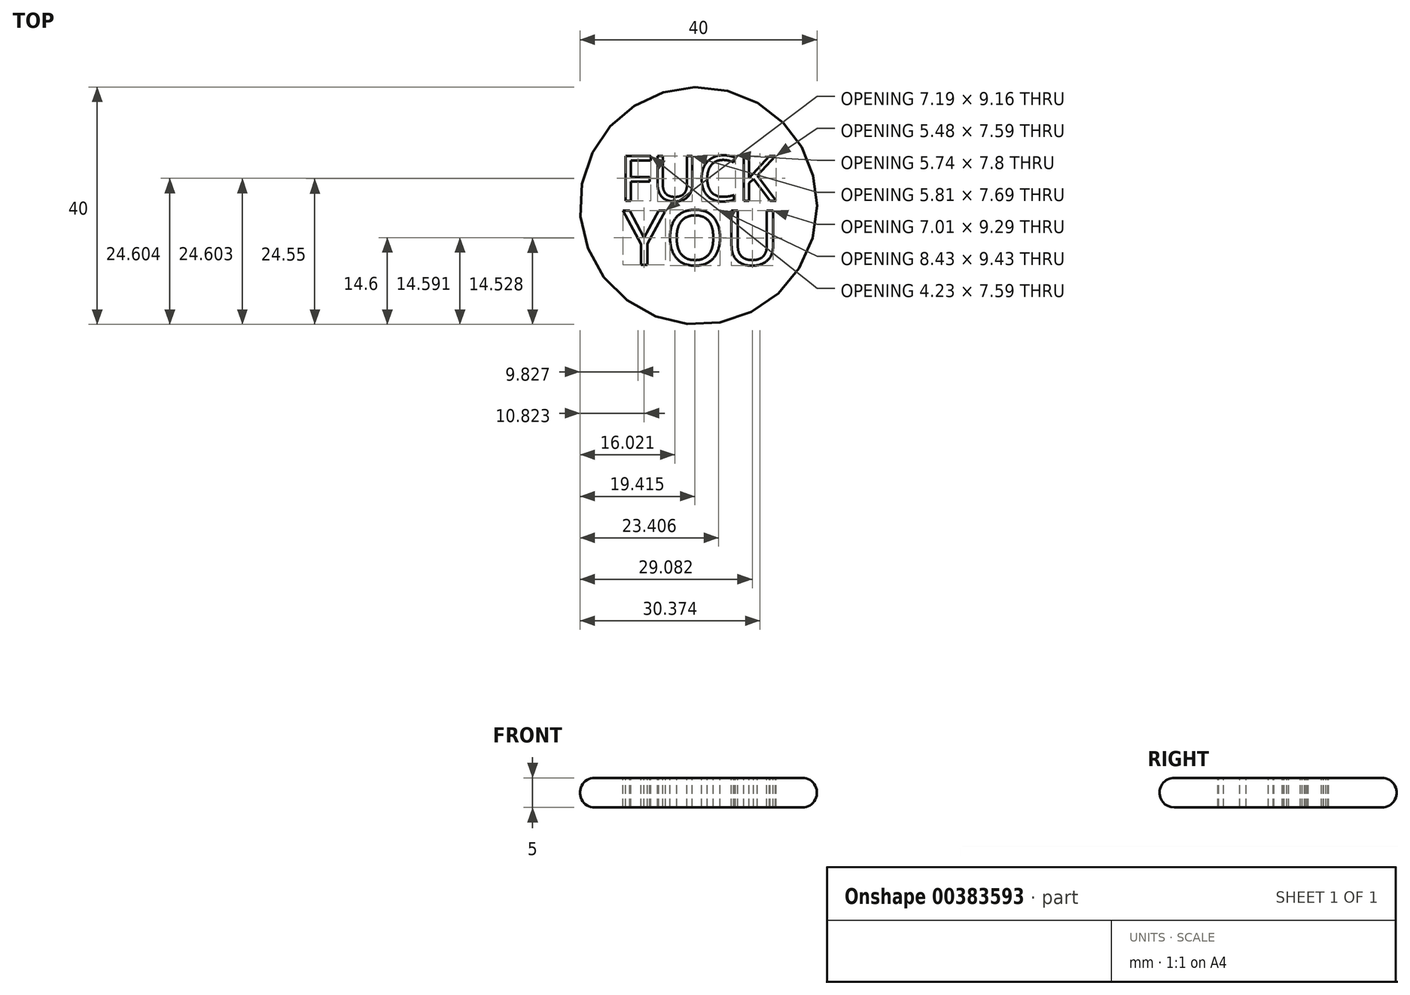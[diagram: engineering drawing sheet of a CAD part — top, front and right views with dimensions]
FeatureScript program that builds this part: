
annotation { "Feature Type Name" : "Feature", "Feature Type Description" : "" }
export const myFeature = defineFeature(function(context is Context, id is Id, definition is map)
    precondition{}
    {
        {
            var Q0;
            Q0=qCreatedBy(makeId("Front.planeOp"),FACE);
            var sketch = newSketch(context, id + "F0", { "sketchPlane" : qUnion([Q0])});
            skLineSegment(sketch, "E0", {"start": v(-17.5, 2.5) * mm, "end": v(0, 2.5) * mm});
            skLineSegment(sketch, "E1", {"start": v(-17.5, -2.5) * mm, "end": v(0, -2.5) * mm});
            skLineSegment(sketch, "E2", {"start": v(0, 2.5) * mm, "end": v(0, -2.5) * mm});
            skPoint(sketch, "E3.center.orphan", {"position": v(-17.5, 0) * mm});
            skArc(sketch, "E4", {"start": v(-17.5, 2.5) * mm, "mid": v(-20, 0) * mm, "end": v(-17.5, -2.5) * mm});
            skSolve(sketch);
        }
        {
            var Q0;
            Q0=makeQuery(id+"F0.imprint","IMPRINT",FACE,{"disambiguationData":[TD([[makeQuery(id+"F0.imprint","IMPRINT",EDGE,{"derivedFrom":sQuery(id+"F0.wireOp",EDGE,"E0")}),-1.0]])]});
            var Q1;
            Q1=sQuery(id+"F0.wireOp",EDGE,"E2");
            revolve(context, id + "F1", {"entities" : qUnion([Q0]), "axis" : qUnion([Q1]), "revolveType" : RevolveType.FULL});
        }
        {
            var Q0;
            Q0=qCreatedBy(makeId("Top.planeOp"),FACE);
            var sketch = newSketch(context, id + "F2", { "sketchPlane" : qUnion([Q0])});
            skText(sketch, "E5", { "text": "FUCK", "fontName": "OpenSans-Regular.ttf"});
            skText(sketch, "E6", { "text": "YOU", "fontName": "OpenSans-Regular.ttf"});
            const initialGuessF2  = {"E5": [-0.01333, 0.00081, 1, 0, 0.00765], "E6": [-0.01277, -0.00999, 1, 0, 0.00924]};
            skSetInitialGuess(sketch, initialGuessF2);
            skSolve(sketch);
        }
        {
            var Q0;
            Q0 = qSketchRegion(id + "F2", true);
            extrude(context, id + "F3", {"entities" : qUnion([Q0]), "operationType" : NewBodyOperationType.REMOVE, "oppositeDirection" : true, "depth" : 25 * mm});
        }
        {
            var Q0;
            Q0 = qSketchRegion(id + "F2", true);
            extrude(context, id + "F4", {"entities" : qUnion([Q0]), "operationType" : NewBodyOperationType.REMOVE, "depth" : 25 * mm});
        }
    });
